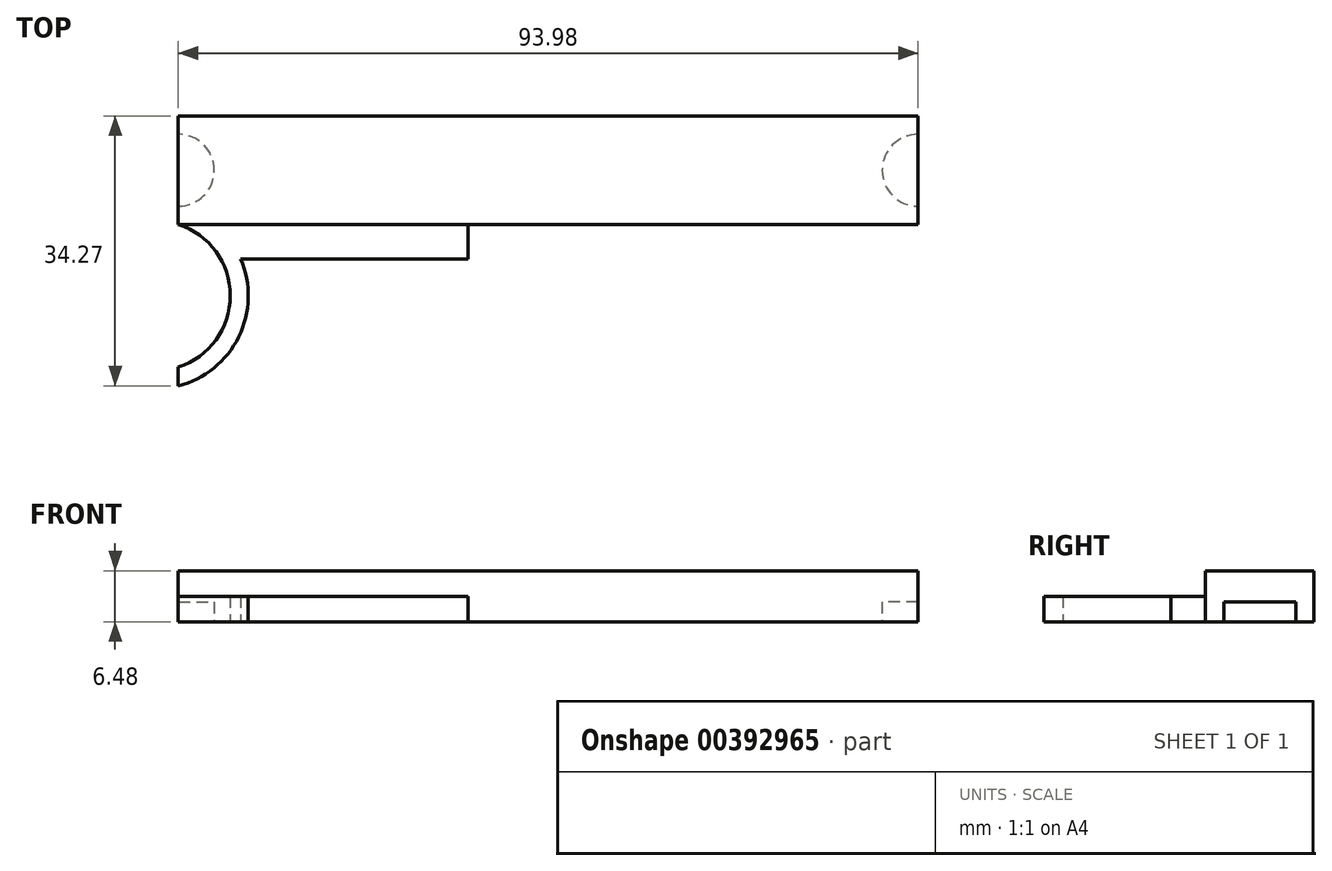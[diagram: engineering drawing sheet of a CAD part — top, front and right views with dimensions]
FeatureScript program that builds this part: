
annotation { "Feature Type Name" : "Feature", "Feature Type Description" : "" }
export const myFeature = defineFeature(function(context is Context, id is Id, definition is map)
    precondition{}
    {
        {
            var Q0;
            Q0=qCreatedBy(makeId("Top.planeOp"),FACE);
            var sketch = newSketch(context, id + "F0", { "sketchPlane" : qUnion([Q0])});
            skLineSegment(sketch, "E0.bottom", {"start": v(-47, 18.16) * mm, "end": v(47, 18.16) * mm});
            skLineSegment(sketch, "E0.top", {"start": v(-39.06, 0) * mm, "end": v(-10.16, 0) * mm});
            skLineSegment(sketch, "E0.left", {"start": v(-47, 18.16) * mm, "end": v(-47, 4.4) * mm});
            skLineSegment(sketch, "E0.right", {"start": v(47, 18.16) * mm, "end": v(47, 4.4) * mm});
            skArc(sketch, "E1", {"start": v(-47, -13.73) * mm, "mid": v(-40.39, -4.66) * mm, "end": v(-47, 4.4) * mm});
            skArc(sketch, "E2", {"start": v(-47, -16.1) * mm, "mid": v(-39.31, -9.88) * mm, "end": v(-39.06, 0) * mm});
            skArc(sketch, "E3.MirrorCS", {"start": v(47, -16.1) * mm, "mid": v(39.31, -9.88) * mm, "end": v(39.06, 0) * mm});
            skArc(sketch, "E4.MirrorCS", {"start": v(47, -13.73) * mm, "mid": v(40.39, -4.66) * mm, "end": v(47, 4.4) * mm});
            skPoint(sketch, "E5.orphan", {"position": v(47, 0) * mm});
            skLineSegment(sketch, "E6.bottom", {"start": v(10.16, 4.4) * mm, "end": v(-10.16, 4.4) * mm});
            skLineSegment(sketch, "E6.left", {"start": v(10.16, 4.4) * mm, "end": v(10.16, 0) * mm});
            skLineSegment(sketch, "E6.right", {"start": v(-10.16, 4.4) * mm, "end": v(-10.16, 0) * mm});
            skPoint(sketch, "E6.middle", {"position": v(0, 0) * mm});
            skPoint(sketch, "E7.orphan", {"position": v(10.16, -4.4) * mm});
            skPoint(sketch, "E8.orphan", {"position": v(-10.16, -4.4) * mm});
            skLineSegment(sketch, "E9.trimOffspring", {"start": v(10.16, 0) * mm, "end": v(39.06, 0) * mm});
            skLineSegment(sketch, "E10.top", {"start": v(-47, 4.4) * mm, "end": v(47, 4.4) * mm});
            skLineSegment(sketch, "E11", {"start": v(-47, -13.73) * mm, "end": v(-47, -16.1) * mm});
            skLineSegment(sketch, "E12", {"start": v(47, 4.4) * mm, "end": v(47, 0) * mm});
            skLineSegment(sketch, "E13.trimOffspring", {"start": v(47, -13.73) * mm, "end": v(47, -16.1) * mm});
            skSolve(sketch);
        }
        {
            var Q0;
            Q0=makeQuery(id+"F0.imprint","IMPRINT",FACE,{"disambiguationData":[TD([[makeQuery(id+"F0.imprint","IMPRINT",EDGE,{"derivedFrom":sQuery(id+"F0.wireOp",EDGE,"E0.bottom")}),-1.0]])]});
            extrude(context, id + "F1", {"entities" : qUnion([Q0]), "depth" : 6.48 * mm, "offsetDistance" : 25.4 * mm});
        }
        {
            var Q0;
            Q0=makeQuery(id+"F0.imprint","IMPRINT",FACE,{"disambiguationData":[TD([[makeQuery(id+"F0.imprint","IMPRINT",EDGE,{"derivedFrom":sQuery(id+"F0.wireOp",EDGE,"E0.top")}),1.0]])]});
            var Q1;
            Q1=makeQuery(id+"F0.imprint","IMPRINT",FACE,{"disambiguationData":[TD([[makeQuery(id+"F0.imprint","IMPRINT",EDGE,{"derivedFrom":sQuery(id+"F0.wireOp",EDGE,"E3.MirrorCS")}),-1.0]])]});
            extrude(context, id + "F2", {"entities" : qUnion([Q0, Q1]), "operationType" : NewBodyOperationType.ADD, "depth" : 3.25 * mm, "offsetDistance" : 25.4 * mm});
        }
        {
            var Q0;
            Q0=makeQuery(id+"F0.imprint","IMPRINT",FACE,{"disambiguationData":[TD([[makeQuery(id+"F0.imprint","IMPRINT",EDGE,{"derivedFrom":sQuery(id+"F0.wireOp",EDGE,"E0.bottom")}),-1.0]])]});
            var sketch = newSketch(context, id + "F3", { "sketchPlane" : qUnion([Q0])});
            skArc(sketch, "E14", {"start": v(-47, 6.7) * mm, "mid": v(-42.42, 11.28) * mm, "end": v(-47, 15.85) * mm});
            skLineSegment(sketch, "E15", {"start": v(-47, 15.85) * mm, "end": v(-47, 6.7) * mm});
            skArc(sketch, "E16.MirrorCS", {"start": v(47, 6.7) * mm, "mid": v(42.42, 11.28) * mm, "end": v(47, 15.85) * mm});
            skLineSegment(sketch, "E17.MirrorCS", {"start": v(47, 15.85) * mm, "end": v(47, 6.7) * mm});
            skSolve(sketch);
        }
        {
            var Q0;
            Q0=qSketchRegion(id+"F3",true);
            extrude(context, id + "F4", {"entities" : qUnion([Q0]), "operationType" : NewBodyOperationType.REMOVE, "depth" : 2.54 * mm, "offsetDistance" : 25.4 * mm});
        }
    });
